# Revit family: 94540063
name_source: partatom
category: Modelos genéricos
revit_build: Autodesk Revit 2016 (Build: 20150220_1215(x64)
units: mm (PartAtom-declared; Revit-internal decimal feet)

## family parameters
Com base no plano de trabalho = Não
Compartilhado = Não
Corte com vazios quando carregados = Não
Cota do conector redondo = Utilizar diâmetro
Pode hospedar o vergalhão = Não
Ponto de cálculo do ambiente = Não
Sempre na vertical = Sim
Tipo de parte = Normal

## types (1)
- Tramontina - Luz 94540/063
    Acabamento = Polido
    Comentários de tipos = Ler Manual de Instalação
    Código de montagem = Tramontina - Luz 94540/063
    Descrição = Tramontina - Luz 94540/063
    Desenvolvedor = Factory Cursos & Desenvolvimento
    Fabricante = Tramontina
    Referencia = Tramontina - Luz 94540/063
    Site do desenvolvedor = www.factorycursos.com.br
    Tipo de imagem = <Nenhum>
    URL = www.tramontina.com.br

## geometry (parser evidence)
native form markers: Blend x2
no freeform markers — native parametric forms only
